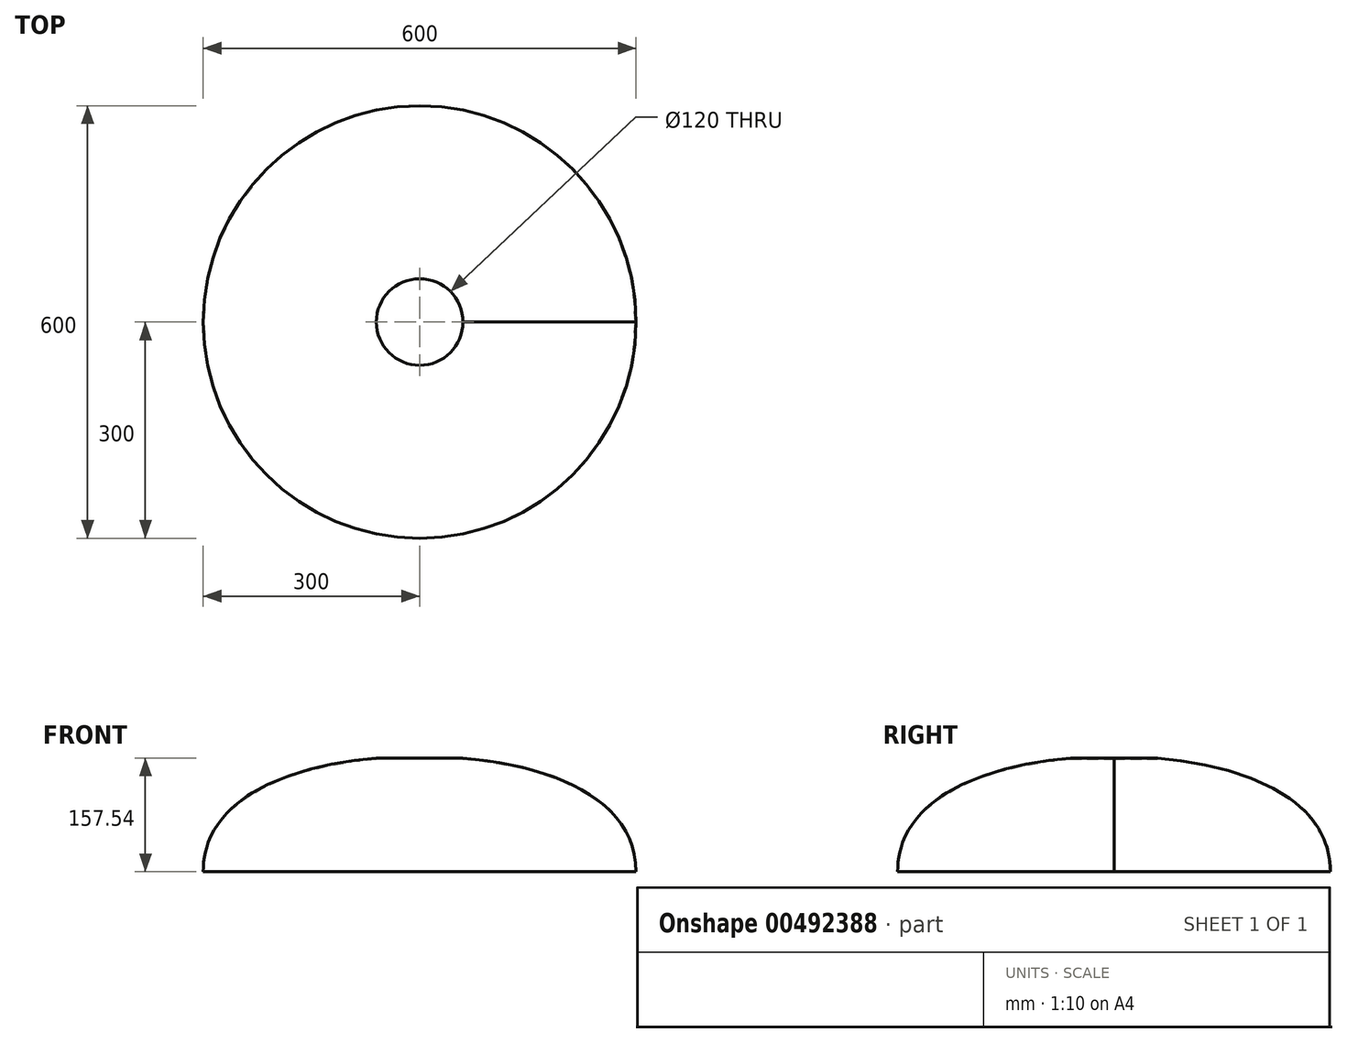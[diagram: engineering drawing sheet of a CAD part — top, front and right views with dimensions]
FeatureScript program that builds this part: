
annotation { "Feature Type Name" : "Feature", "Feature Type Description" : "" }
export const myFeature = defineFeature(function(context is Context, id is Id, definition is map)
    precondition{}
    {
        {
            var Q0;
            Q0=qCreatedBy(makeId("Right.planeOp"),FACE);
            var sketch = newSketch(context, id + "F0", { "sketchPlane" : qUnion([Q0])});
            skLineSegment(sketch, "E0", {"start": v(0, 0) * mm, "end": v(300, 0) * mm});
            skLineSegment(sketch, "E1", {"start": v(0, 160) * mm, "end": v(0, 0) * mm});
            skFitSpline(sketch, "E2", {"points": [v(0, 160) * mm, v(300, 0) * mm], "startDerivative": vector(480, 0) * mm, "endDerivative": vector(0, -330) * mm});
            skLineSegment(sketch, "E3", {"start": v(0, 160) * mm, "end": v(300, 160) * mm, "construction": true});
            skLineSegment(sketch, "E4", {"start": v(300, 160) * mm, "end": v(300, 0) * mm, "construction": true});
            skSolve(sketch);
        }
        {
            var Q0;
            Q0=qSketchRegion(id+"F0",true);
            var Q1;
            Q1=sQuery(id+"F0.wireOp",EDGE,"E1");
            revolve(context, id + "F1", {"entities" : qUnion([Q0]), "axis" : qUnion([Q1]), "revolveType" : RevolveType.FULL});
        }
        {
            var Q0;
            Q0=makeQuery(id+"F1.opRevolve","SWEPT_FACE",FACE,{"disambiguationData":[OSD([sQuery(id+"F0.wireOp",EDGE,"E0")])]});
            shell(context, id + "F2", {"entities" : qUnion([Q0]), "thickness" : 1 * mm});
        }
        {
            var Q0;
            Q0=qCreatedBy(makeId("Top.planeOp"),FACE);
            var sketch = newSketch(context, id + "F3", { "sketchPlane" : qUnion([Q0])});
            skCircle(sketch, "E5", {"center": v(0, 0) * mm, "radius": 60 * mm});
            skSolve(sketch);
        }
        {
            var Q0;
            Q0=qSketchRegion(id+"F3",true);
            extrude(context, id + "F4", {"entities" : qUnion([Q0]), "operationType" : NewBodyOperationType.REMOVE, "endBound" : BoundingType.THROUGH_ALL, "depth" : 25 * mm});
        }
    });
